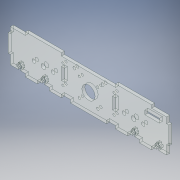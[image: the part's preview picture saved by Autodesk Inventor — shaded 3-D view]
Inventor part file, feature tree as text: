
AUTODESK INVENTOR PART (.ipt)
format: ipt  version: 2019 (Build 230136000, 136)  size: 676,864 bytes
history: native  units: mm
features: extrude x11, sketch x11, projected_geometry x11
ambient origin geometry x8: Origin, YZ Plane, XZ Plane, XY Plane, X Axis, Y Axis, Z Axis, Center Point
bodies: Body1 (feature_tree)
feature tree (33):
  extrude  "Extrusion3"  Depth=50.0mm
  sketch  "Sketch2"  dims[d4=5.0mm d6=50.0mm]
  extrude  "Extrusion6"  Depth=50.0mm
  extrude  "Extrusion7"  Depth=50.0mm
  extrude  "Extrusion9"  Depth=6.0mm
  extrude  "Extrusion11"  Depth=6.0mm
  extrude  "Extrusion12"  Depth=32.0mm
  extrude  "Extrusion13"  Depth=59.0mm
  extrude  "Extrusion14"  Depth=8.0mm
  extrude  "Extrusion16"  Depth=16.0mm
  extrude  "Extrusion17"  Depth=10.0mm
  extrude  "Extrusion18"  Depth=5.0mm
  sketch  "Sketch1"  dims[d0=300.0mm d3=50.0mm]
  projected_geometry  "Projected Loop1"
  sketch  "Sketch4"  dims[d8=50.0mm d9=50.0mm]
  projected_geometry  "Projected Loop2"
  sketch  "Sketch7"  dims[d12=6.0mm d13=6.0mm]
  projected_geometry  "Projected Loop10"
  projected_geometry  "Projected Loop11"
  projected_geometry  "Projected Loop12"
  sketch  "Sketch12"  dims[d14=32.0mm d15=6.0mm]
  projected_geometry  "Projected Loop17"
  sketch  "Sketch13"  dims[d16=6.0mm d17=32.0mm]
  projected_geometry  "Projected Loop18"
  sketch  "Sketch14"  dims[d18=59.0mm d19=59.0mm]
  projected_geometry  "Projected Loop19"
  sketch  "Sketch15"  dims[d22=8.0mm d23=8.0mm]
  projected_geometry  "Projected Loop20"
  sketch  "Sketch16"  dims[d24=16.0mm d25=16.0mm]
  sketch  "Sketch17"  dims[d26=5.0mm d27=0.0mm d42=10.0mm]
  projected_geometry  "Projected Loop21"
  sketch  "Sketch18"  dims[d43=5.0mm d44=5.0mm d45=5.0mm d46=0.0mm d48=5.0mm d50=40.0mm d51=5.0mm d52=0.0mm d55=5.0mm d56=0.0mm d57=45.0mm d58=90.0mm d59=45.0mm d79=20.0mm d80=20.0mm d81=5.0mm d82=0.0mm d83=5.0mm d84=5.0mm d85=20.0mm d86=20.0mm d87=20.0mm d88=20.0mm d89=5.0mm d90=0.0mm d91=8.0mm d92=4.0mm d93=10.0mm d94=8.0mm d95=4.0mm d96=5.0mm d97=0.0mm d98=20.0mm d103=15.0mm d104=6.0mm d105=6.0mm d106=4.0mm d107=4.0mm d108=47.0mm d109=47.0mm d110=5.0mm d111=5.0mm d112=5.0mm d113=5.0mm d114=60.0mm d115=5.0mm d116=15.0mm d117=5.0mm d118=0.0mm d119=47.0mm d120=47.0mm d121=5.0mm d122=5.0mm d125=60.0mm d126=5.0mm d127=15.0mm d130=5.0mm d131=0.0mm d132=3.5mm d133=30.0mm d134=10.0mm d135=5.0mm d136=0.0mm d137=24.0mm d138=7.0mm d139=12.0mm d140=8.0mm d141=5.0mm d142=0.0mm]
  projected_geometry  "Projected Loop22"
